# Revit family: Specialty_Equipment-Fiberglass_Planter-Planters_Unlimited-Nazca-Round
name_source: partatom
category: Specialty Equipment
units: mm (PartAtom-declared; Revit-internal decimal feet)

## family parameters
Always vertical = Yes
Cut with Voids When Loaded = No
Enable Cutting in Views = No
Maintain Annotation Orientation = No
OmniClass Number = 23.40.05.21.17
OmniClass Title = Planters
Part Type = Normal
Room Calculation Point = No
Round Connector Dimension = Use Diameter
Shared = No
Work Plane-Based = No

## types (6) — shared parameters
Assembly Code = G2050600
CD_Cut angle = 45.51°
CD_Finish = Plastic-Fiberglass-Carlsbad-Semi_Gloss-Charcoal
CD_Microsite = https://www.caddetails.com
CD_Product Page URL = https://www.plantersunlimited.com
CD_Specification = https://www.plantersunlimited.com
Default Elevation = 0.0"
Description = Nazca Round Planter
Manufacturer = Planters Unlimited
Model = Nazca Series Planter
Type Comments = Round Planter
URL = https://www.plantersunlimited.com

## per-type parameters (varying)
| type | CD_Base Dia | CD_Diameter | CD_Height | CD_Lip Width | CD_Pad Spacing | CD_Top Lip |
| 20"Dia x 30"H | 6.7" | 20.0" | 30.0" | 17.0" | 4.7" | 5.0" |
| 24"Dia x 24"H | 8.0" | 24.0" | 24.0" | 21.0" | 6.0" | 6.0" |
| 24"Dia x 30"H | 8.0" | 24.0" | 30.0" | 21.0" | 6.0" | 6.0" |
| 24"Dia x 36"H | 8.0" | 24.0" | 36.0" | 21.0" | 6.0" | 6.0" |
| 36"Dia x 48"H | 12.0" | 36.0" | 48.0" | 33.0" | 10.0" | 9.0" |
| 48"Dia x 30"H | 16.0" | 48.0" | 30.0" | 45.0" | 14.0" | 12.0" |

## geometry (parser evidence)
native form markers: Sweep x4
no freeform markers — native parametric forms only
